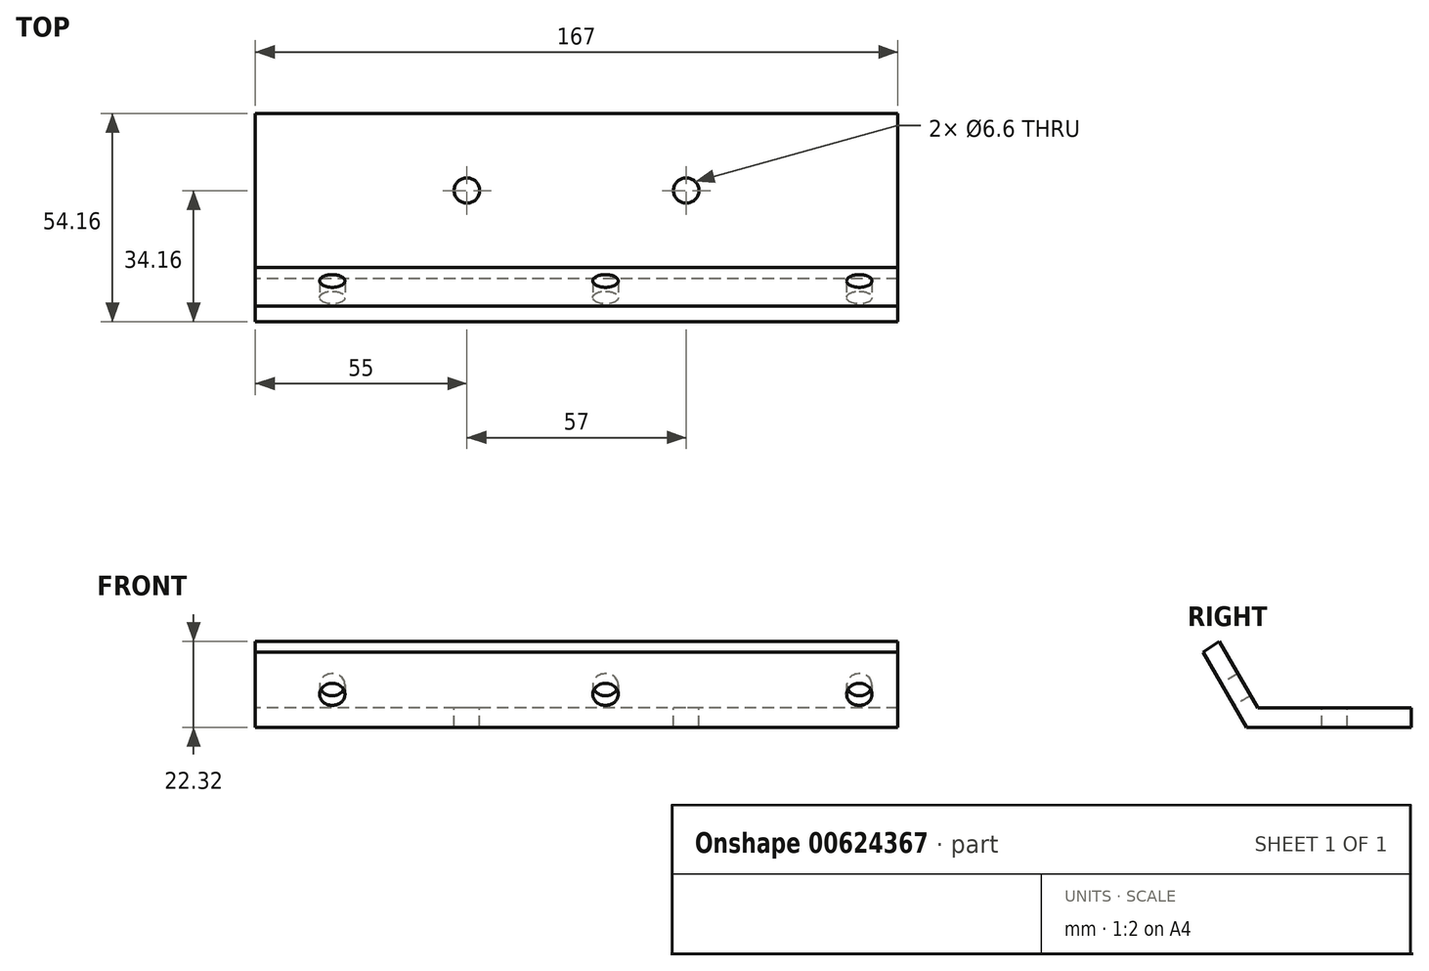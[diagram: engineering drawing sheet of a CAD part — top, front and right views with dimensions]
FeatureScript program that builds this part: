
annotation { "Feature Type Name" : "Feature", "Feature Type Description" : "" }
export const myFeature = defineFeature(function(context is Context, id is Id, definition is map)
    precondition{}
    {
        {
            var Q0;
            Q0=qCreatedBy(makeId("Right.planeOp"),FACE);
            var sketch = newSketch(context, id + "F0", { "sketchPlane" : qUnion([Q0])});
            skLineSegment(sketch, "E0.bottom", {"start": v(20, 0) * mm, "end": v(-22.87, 0) * mm});
            skLineSegment(sketch, "E0.top", {"start": v(20, 5) * mm, "end": v(-20, 5) * mm});
            skLineSegment(sketch, "E0.left", {"start": v(20, 0) * mm, "end": v(20, 5) * mm});
            skLineSegment(sketch, "E1", {"start": v(-20, 5) * mm, "end": v(-30, 22.32) * mm});
            skLineSegment(sketch, "E2", {"start": v(-22.87, 0) * mm, "end": v(-34.16, 19.54) * mm});
            skLineSegment(sketch, "E3", {"start": v(-34.16, 19.54) * mm, "end": v(-30, 22.32) * mm});
            skSolve(sketch);
        }
        {
            var Q0;
            Q0=makeQuery(id+"F0.imprint","IMPRINT",FACE,{"disambiguationData":[TD([[makeQuery(id+"F0.imprint","IMPRINT",EDGE,{"derivedFrom":sQuery(id+"F0.wireOp",EDGE,"E0.bottom")}),-1.0]])]});
            extrude(context, id + "F1", {"entities" : qUnion([Q0]), "depth" : 167 * mm, "offsetDistance" : 25 * mm});
        }
        {
            var Q0;
            Q0=makeQuery(id+"F1.opExtrude","SWEPT_FACE",FACE,{"disambiguationData":[OSD([sQuery(id+"F0.wireOp",EDGE,"E0.top")])]});
            var sketch = newSketch(context, id + "F2", { "sketchPlane" : qUnion([Q0])});
            skPoint(sketch, "E4", {"position": v(112, 0) * mm});
            skPoint(sketch, "E5", {"position": v(55, 0) * mm});
            skSolve(sketch);
        }
        {
            var Q0;
            Q0=sQuery(id+"F2.wireOp",VERTEX,"E4");
            var Q1;
            Q1=sQuery(id+"F2.wireOp",VERTEX,"E5");
            var Q2;
            Q2=makeQuery(id+"F1.opExtrude","SWEPT_BODY",BODY,{"disambiguationData":[OSD([sQuery(id+"F0.wireOp",EDGE,"E0.bottom"),sQuery(id+"F0.wireOp",EDGE,"E0.top"),sQuery(id+"F0.wireOp",EDGE,"E0.left"),sQuery(id+"F0.wireOp",EDGE,"E1"),sQuery(id+"F0.wireOp",EDGE,"E2"),sQuery(id+"F0.wireOp",EDGE,"E3")])]});
            hole(context, id + "F3", {"style" : HoleStyle.SIMPLE, "endStyle" : HoleEndStyle.THROUGH, "standardTappedOrClearance" : lookupTablePath({ "standard" : "ISO", "fit" : "Normal", "size" : "M6", "type" : "Clearance" }), "standardBlindInLast" : lookupTablePath({ "fit" : "Standard", "standard" : "ISO", "size" : "M6", "type" : "Clearance" }), "holeDiameter" : 6.6 * mm, "majorDiameter" : 5 * mm, "isTappedThrough" : true, "tappedDepth" : 12 * mm, "tapClearance" : 3, "locations" : qUnion([Q0, Q1]), "scope" : qUnion([Q2])});
        }
        {
            var Q0;
            Q0=makeQuery(id+"F1.opExtrude","SWEPT_FACE",FACE,{"disambiguationData":[OSD([sQuery(id+"F0.wireOp",EDGE,"E2")])]});
            var sketch = newSketch(context, id + "F4", { "sketchPlane" : qUnion([Q0])});
            skPoint(sketch, "E6", {"position": v(20, 21.33) * mm});
            skPoint(sketch, "E7", {"position": v(91, 21.33) * mm});
            skPoint(sketch, "E8", {"position": v(157, 21.33) * mm});
            skSolve(sketch);
        }
        {
            var Q0;
            Q0=sQuery(id+"F4.wireOp",VERTEX,"E6");
            var Q1;
            Q1=sQuery(id+"F4.wireOp",VERTEX,"E7");
            var Q2;
            Q2=sQuery(id+"F4.wireOp",VERTEX,"E8");
            var Q3;
            Q3=makeQuery(id+"F1.opExtrude","SWEPT_BODY",BODY,{"disambiguationData":[OSD([sQuery(id+"F0.wireOp",EDGE,"E0.bottom"),sQuery(id+"F0.wireOp",EDGE,"E0.top"),sQuery(id+"F0.wireOp",EDGE,"E0.left"),sQuery(id+"F0.wireOp",EDGE,"E1"),sQuery(id+"F0.wireOp",EDGE,"E2"),sQuery(id+"F0.wireOp",EDGE,"E3")])]});
            hole(context, id + "F5", {"style" : HoleStyle.SIMPLE, "endStyle" : HoleEndStyle.THROUGH, "standardTappedOrClearance" : lookupTablePath({ "standard" : "ISO", "fit" : "Normal", "size" : "M6", "type" : "Clearance" }), "standardBlindInLast" : lookupTablePath({ "fit" : "Standard", "standard" : "ISO", "size" : "M6", "type" : "Clearance" }), "holeDiameter" : 6.6 * mm, "majorDiameter" : 5 * mm, "isTappedThrough" : true, "tappedDepth" : 12 * mm, "tapClearance" : 3, "locations" : qUnion([Q0, Q1, Q2]), "scope" : qUnion([Q3])});
        }
    });
